# Revit family: xBath_Shower-American_Standard- Fluent-T186_Series
name_source: partatom
category: Plumbing Fixtures
revit_build: Autodesk Revit 2014 (Build: 20130308_1515(x64)
units: mm (PartAtom-declared; Revit-internal decimal feet)

## types (3) — shared parameters
ADA Compliant = Yes
Assembly Code = D2010710
CW Connection = Yes
CWFU = 3
Default Elevation = 0"
Description = Fluent Pressure Balance Bath/Shower Fitting,
Diverter = Yes
Finish = Metal-American Standard-002-Polished Chrome
Flow Rate = 2.5 gpm/9.5 L/min.
HW Connection = Yes
HWFU = 3
Height = 3 7/8"
Installation Type = Wall Mounted
Length = 3 7/8"
Manufacturer = American Standard
Material = Metal-American Standard-002-Polished Chrome
Price = Prices may vary. Please consult Manufacturer Representative for most up-to-date price list.
Product Documentation Link = https://www.americanstandard-us.com
Product Page URL = https://www.americanstandard-us.com
Spacing from Wall = 2 5/8"
Specification = SUGGESTED SPECIFICATION Bath/shower fitting shall feature brass square rain showerhead with Max. 2.5 gpm/9.5 L/min. flow rate.
URL = https://www.americanstandard-us.com
Vent Connection = No
WFU = 4
Warranty Information = Limited Lifetime Function and Finish Warranty
Waste Connection = No
Water Connection Diameter = 1/2"
Width = 1 15/16"

## per-type parameters (varying)
| type | Diverter_Shower Connection | Diverter_Shower Outlet Description | Diverter_Spout Connection | Diverter_Spout Outlet Description | Shower | Shower Connection Description | Shower Connection Size | Shower Kit | Spout | Spout Connection Description | Spout Connection Size | Spout Kit |
| T186.502 | 1/2" | 1/2'' Global Outlet Connection | 1/2" | 1/2'' Global Outlet Connection | Yes | 1/2'' Global NPT Inlet Connection | 1/2" | Yes | Yes | 1/2'' Global Inlet Connection | 1/2" | Yes |
| T186.501 | 1/2" | 1/2'' Global Outlet Connection | 0" |  | Yes | 1/2'' Global NPT Inlet Connection | 1/2" | Yes | No |  | 0" | No |
| T186.500 | 0" |  | 0" |  | No |  | 0" | No | No |  | 0" | No |

note: column(s) folded — value = type name in every type: Model

## geometry (parser evidence)
native form markers: Sweep x1
no freeform markers — native parametric forms only
